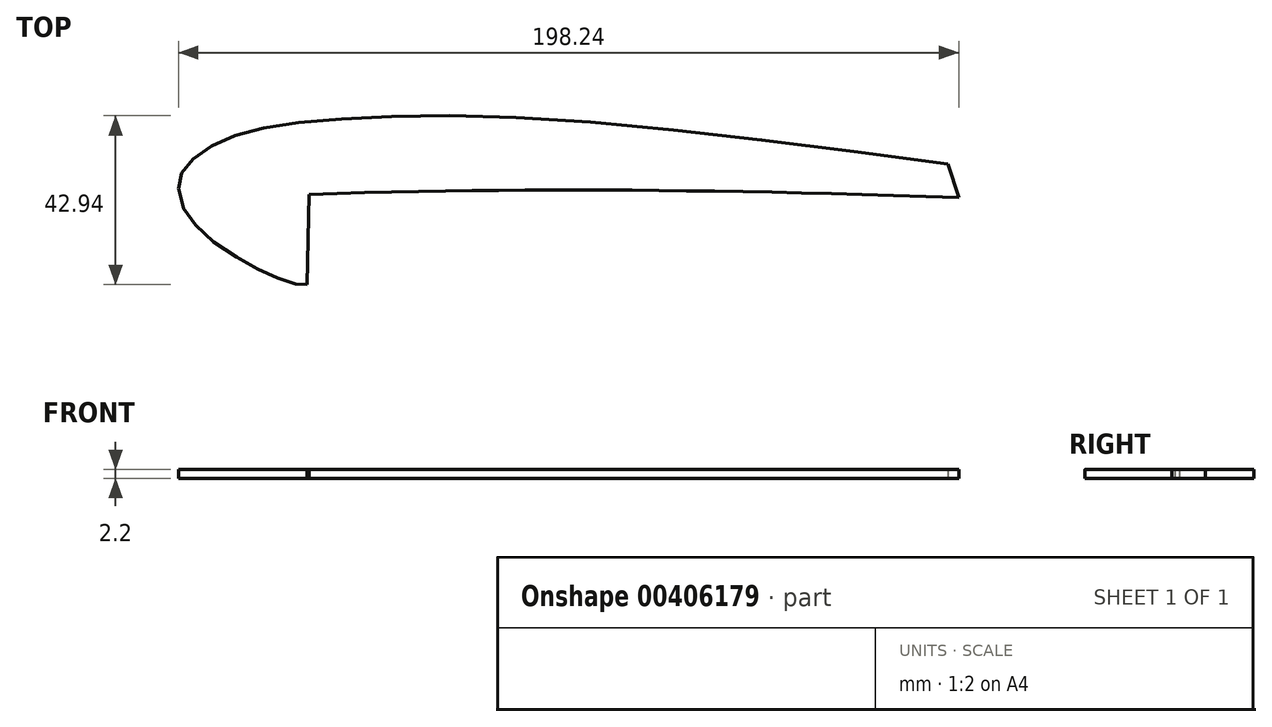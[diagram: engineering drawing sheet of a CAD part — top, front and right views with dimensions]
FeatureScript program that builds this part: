
annotation { "Feature Type Name" : "Feature", "Feature Type Description" : "" }
export const myFeature = defineFeature(function(context is Context, id is Id, definition is map)
    precondition{}
    {
        {
            var Q0;
            Q0=qCreatedBy(makeId("Top.planeOp"),FACE);
            var sketch = newSketch(context, id + "F0", { "sketchPlane" : qUnion([Q0])});
            skFitSpline(sketch, "E0", {"points": [v(36.95, -22.04) * mm, v(201.97, -22.83) * mm], "startDerivative": vector(164.03, 5.02) * mm, "endDerivative": vector(195.7, -6.5) * mm});
            skLineSegment(sketch, "E1", {"start": v(201.97, -22.83) * mm, "end": v(199.18, -14.3) * mm});
            skPoint(sketch, "E2.7.internal.snap0", {"position": v(200.58, -18.56) * mm});
            skFitSpline(sketch, "E2", {"points": [v(199.18, -14.3) * mm, v(95.32, -2.79) * mm, v(46.75, -2.79) * mm, v(25.37, -5.2) * mm, v(14.99, -8.34) * mm, v(8.37, -12.24) * mm, v(5.02, -16) * mm, v(3.82, -18.56) * mm, v(4.38, -23.97) * mm, v(6.89, -28.5) * mm, v(12.46, -34.04) * mm, v(20.7, -39.26) * mm, v(26.68, -42.43) * mm, v(32.23, -44.48) * mm, v(35.02, -44.99) * mm, v(36.41, -44.92) * mm], "startDerivative": vector(-551.54, 72.42) * mm, "endDerivative": vector(55.6, 5.47) * mm});
            skLineSegment(sketch, "E3", {"start": v(36.41, -44.92) * mm, "end": v(36.95, -22.04) * mm});
            skSolve(sketch);
        }
        {
            var Q0;
            Q0=makeQuery(id+"F0.imprint","IMPRINT",FACE,{"disambiguationData":[TD([[makeQuery(id+"F0.imprint","IMPRINT",EDGE,{"derivedFrom":sQuery(id+"F0.wireOp",EDGE,"E0")}),1.0]])]});
            extrude(context, id + "F1", {"entities" : qUnion([Q0]), "depth" : 2.2 * mm});
        }
        {
            var Q0;
            Q0=makeQuery(id+"F1.opExtrude","CAP_FACE",FACE,{"disambiguationData":[OSD([sQuery(id+"F0.wireOp",EDGE,"E0"),sQuery(id+"F0.wireOp",EDGE,"E1"),sQuery(id+"F0.wireOp",EDGE,"E2"),sQuery(id+"F0.wireOp",EDGE,"E3")])],"isStart":false});
            cPlane(context, id + "F2", {"entities" : qUnion([Q0]), "cplaneType" : CPlaneType.OFFSET, "offset" : 2 * mm, "width" : 150 * mm, "height" : 150 * mm});
        }
    });
